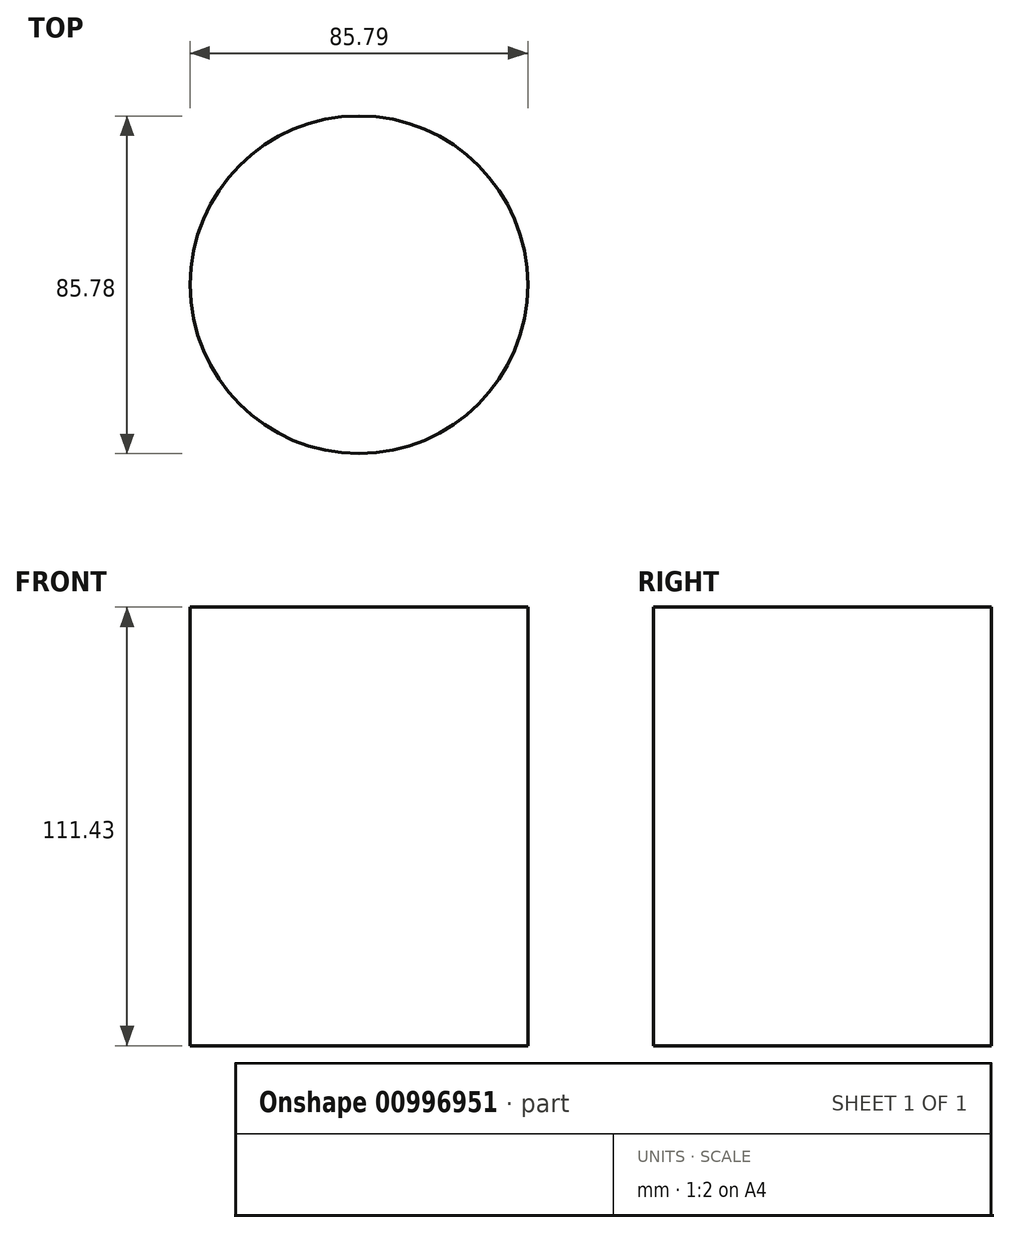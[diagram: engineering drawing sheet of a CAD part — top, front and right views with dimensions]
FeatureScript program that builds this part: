
annotation { "Feature Type Name" : "Feature", "Feature Type Description" : "" }
export const myFeature = defineFeature(function(context is Context, id is Id, definition is map)
    precondition{}
    {
        {
            var Q0;
            Q0=qCreatedBy(makeId("Front.planeOp"),FACE);
            var sketch = newSketch(context, id + "F0", { "sketchPlane" : qUnion([Q0])});
            skLineSegment(sketch, "E0.bottom", {"start": v(-51.9, 53.4) * mm, "end": v(-9, 53.4) * mm});
            skLineSegment(sketch, "E0.top", {"start": v(-51.9, -58.04) * mm, "end": v(-9, -58.04) * mm});
            skLineSegment(sketch, "E0.left", {"start": v(-51.9, 53.4) * mm, "end": v(-51.9, -58.04) * mm});
            skLineSegment(sketch, "E0.right", {"start": v(-9, 53.4) * mm, "end": v(-9, -58.04) * mm});
            skLineSegment(sketch, "E1.MirrorCS", {"start": v(9, 53.4) * mm, "end": v(9, -58.04) * mm});
            skSolve(sketch);
        }
        {
            var Q0;
            Q0=makeQuery(id+"F0.imprint","IMPRINT",FACE,{"disambiguationData":[TD([[makeQuery(id+"F0.imprint","IMPRINT",EDGE,{"derivedFrom":sQuery(id+"F0.wireOp",EDGE,"E0.bottom")}),-1.0]])]});
            var Q1;
            Q1=sQuery(id+"F0.wireOp",EDGE,"E0.left");
            revolve(context, id + "F1", {"surfaceOperationType" : NewSurfaceOperationType.NEW, "entities" : qUnion([Q0]), "axis" : qUnion([Q1]), "revolveType" : RevolveType.FULL});
        }
    });
